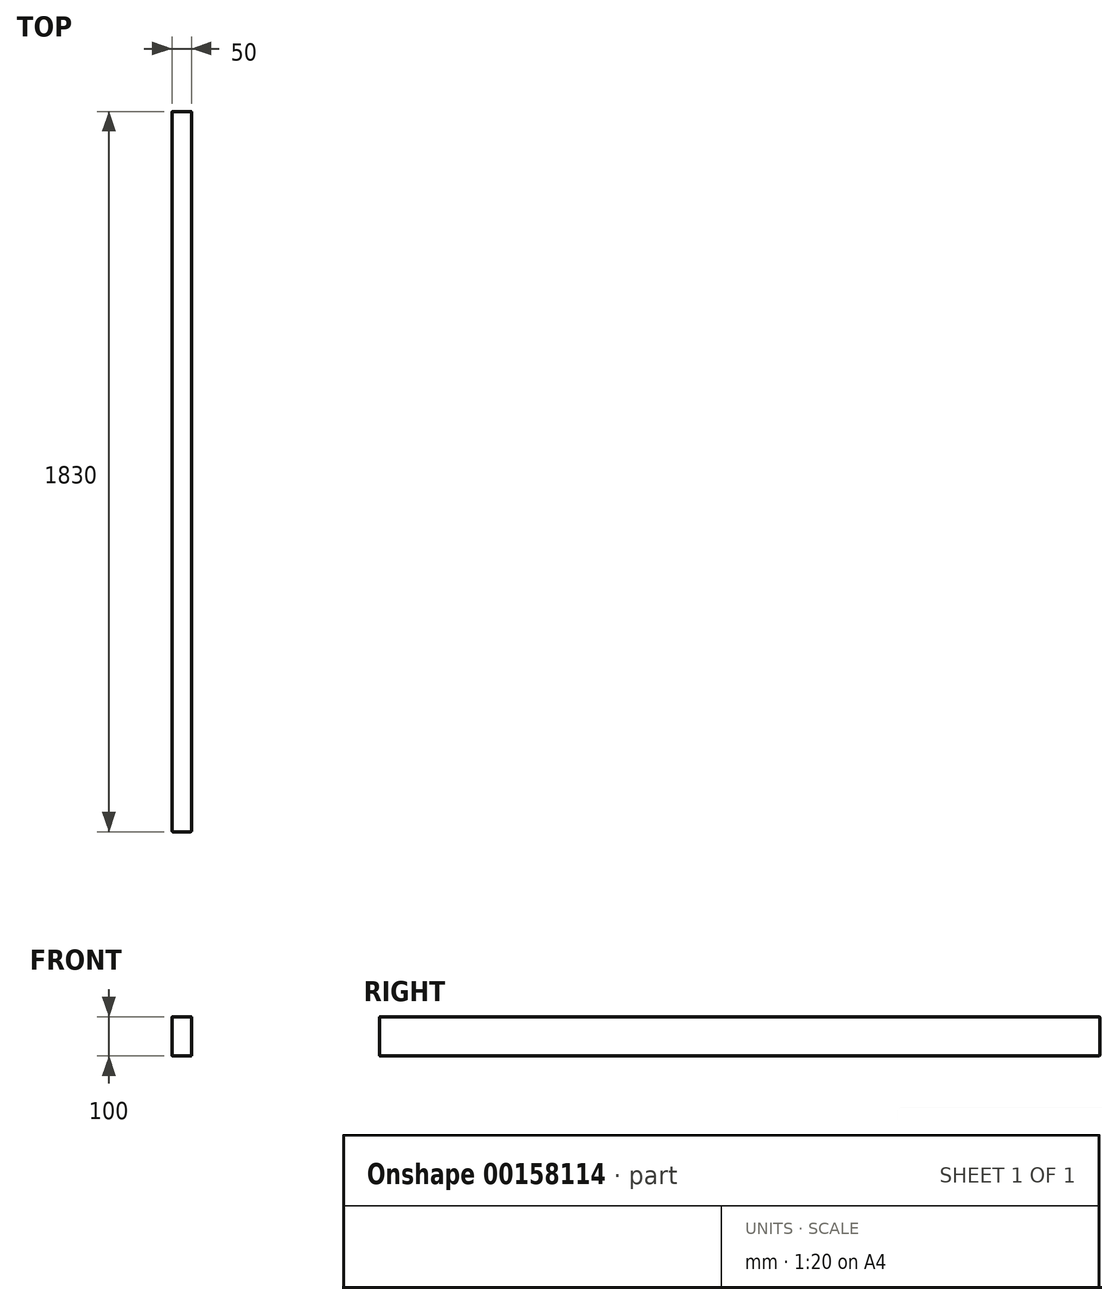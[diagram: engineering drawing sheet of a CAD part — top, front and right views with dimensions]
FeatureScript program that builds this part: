
annotation { "Feature Type Name" : "Feature", "Feature Type Description" : "" }
export const myFeature = defineFeature(function(context is Context, id is Id, definition is map)
    precondition{}
    {
        {
            var Q0;
            Q0=qCreatedBy(makeId("Front.planeOp"),FACE);
            var sketch = newSketch(context, id + "F0", { "sketchPlane" : qUnion([Q0])});
            skLineSegment(sketch, "E0.bottom", {"start": v(25, 50) * mm, "end": v(-25, 50) * mm});
            skLineSegment(sketch, "E0.top", {"start": v(25, -50) * mm, "end": v(-25, -50) * mm});
            skLineSegment(sketch, "E0.left", {"start": v(25, 50) * mm, "end": v(25, -50) * mm});
            skLineSegment(sketch, "E0.right", {"start": v(-25, 50) * mm, "end": v(-25, -50) * mm});
            skPoint(sketch, "E0.middle", {"position": v(0, 0) * mm});
            skSolve(sketch);
        }
        {
            var Q0;
            Q0=makeQuery(id+"F0.imprint","IMPRINT",FACE,{"disambiguationData":[TD([[makeQuery(id+"F0.imprint","IMPRINT",EDGE,{"derivedFrom":sQuery(id+"F0.wireOp",EDGE,"E0.bottom")}),1.0]])]});
            extrude(context, id + "F1", {"entities" : qUnion([Q0]), "endBound" : BoundingType.SYMMETRIC, "depth" : 1830 * mm});
        }
        {
            var Q0;
            Q0=makeQuery(id+"F1.opExtrude","SWEPT_EDGE",EDGE,{"disambiguationData":[OSD([sQuery(id+"F0.wireOp",EDGE,"E0.bottom"),sQuery(id+"F0.wireOp",EDGE,"E0.right")])]});
            var Q1;
            Q1=makeQuery(id+"F1.opExtrude","SWEPT_EDGE",EDGE,{"disambiguationData":[OSD([sQuery(id+"F0.wireOp",EDGE,"E0.bottom"),sQuery(id+"F0.wireOp",EDGE,"E0.left")])]});
            var Q2;
            Q2=makeQuery(id+"F1.opExtrude","SWEPT_EDGE",EDGE,{"disambiguationData":[OSD([sQuery(id+"F0.wireOp",EDGE,"E0.top"),sQuery(id+"F0.wireOp",EDGE,"E0.right")])]});
            var Q3;
            Q3=makeQuery(id+"F1.opExtrude","CAP_EDGE",EDGE,{"disambiguationData":[OSD([sQuery(id+"F0.wireOp",EDGE,"E0.right")])],"isStart":true});
            var Q4;
            Q4=makeQuery(id+"F1.opExtrude","CAP_EDGE",EDGE,{"disambiguationData":[OSD([sQuery(id+"F0.wireOp",EDGE,"E0.bottom")])],"isStart":true});
            var Q5;
            Q5=makeQuery(id+"F1.opExtrude","CAP_EDGE",EDGE,{"disambiguationData":[OSD([sQuery(id+"F0.wireOp",EDGE,"E0.top")])],"isStart":true});
            var Q6;
            Q6=makeQuery(id+"F1.opExtrude","CAP_EDGE",EDGE,{"disambiguationData":[OSD([sQuery(id+"F0.wireOp",EDGE,"E0.left")])],"isStart":true});
            var Q7;
            Q7=makeQuery(id+"F1.opExtrude","SWEPT_EDGE",EDGE,{"disambiguationData":[OSD([sQuery(id+"F0.wireOp",EDGE,"E0.top"),sQuery(id+"F0.wireOp",EDGE,"E0.left")])]});
            var Q8;
            Q8=makeQuery(id+"F1.opExtrude","CAP_EDGE",EDGE,{"disambiguationData":[OSD([sQuery(id+"F0.wireOp",EDGE,"E0.right")])],"isStart":false});
            var Q9;
            Q9=makeQuery(id+"F1.opExtrude","CAP_EDGE",EDGE,{"disambiguationData":[OSD([sQuery(id+"F0.wireOp",EDGE,"E0.bottom")])],"isStart":false});
            var Q10;
            Q10=makeQuery(id+"F1.opExtrude","CAP_EDGE",EDGE,{"disambiguationData":[OSD([sQuery(id+"F0.wireOp",EDGE,"E0.left")])],"isStart":false});
            var Q11;
            Q11=makeQuery(id+"F1.opExtrude","CAP_EDGE",EDGE,{"disambiguationData":[OSD([sQuery(id+"F0.wireOp",EDGE,"E0.top")])],"isStart":false});
            fillet(context, id + "F2", {"entities" : qUnion([Q0, Q1, Q2, Q3, Q4, Q5, Q6, Q7, Q8, Q9, Q10, Q11]), "radius" : 2 * mm, "tangentPropagation" : true, "allowEdgeOverflow" : false});
        }
    });
